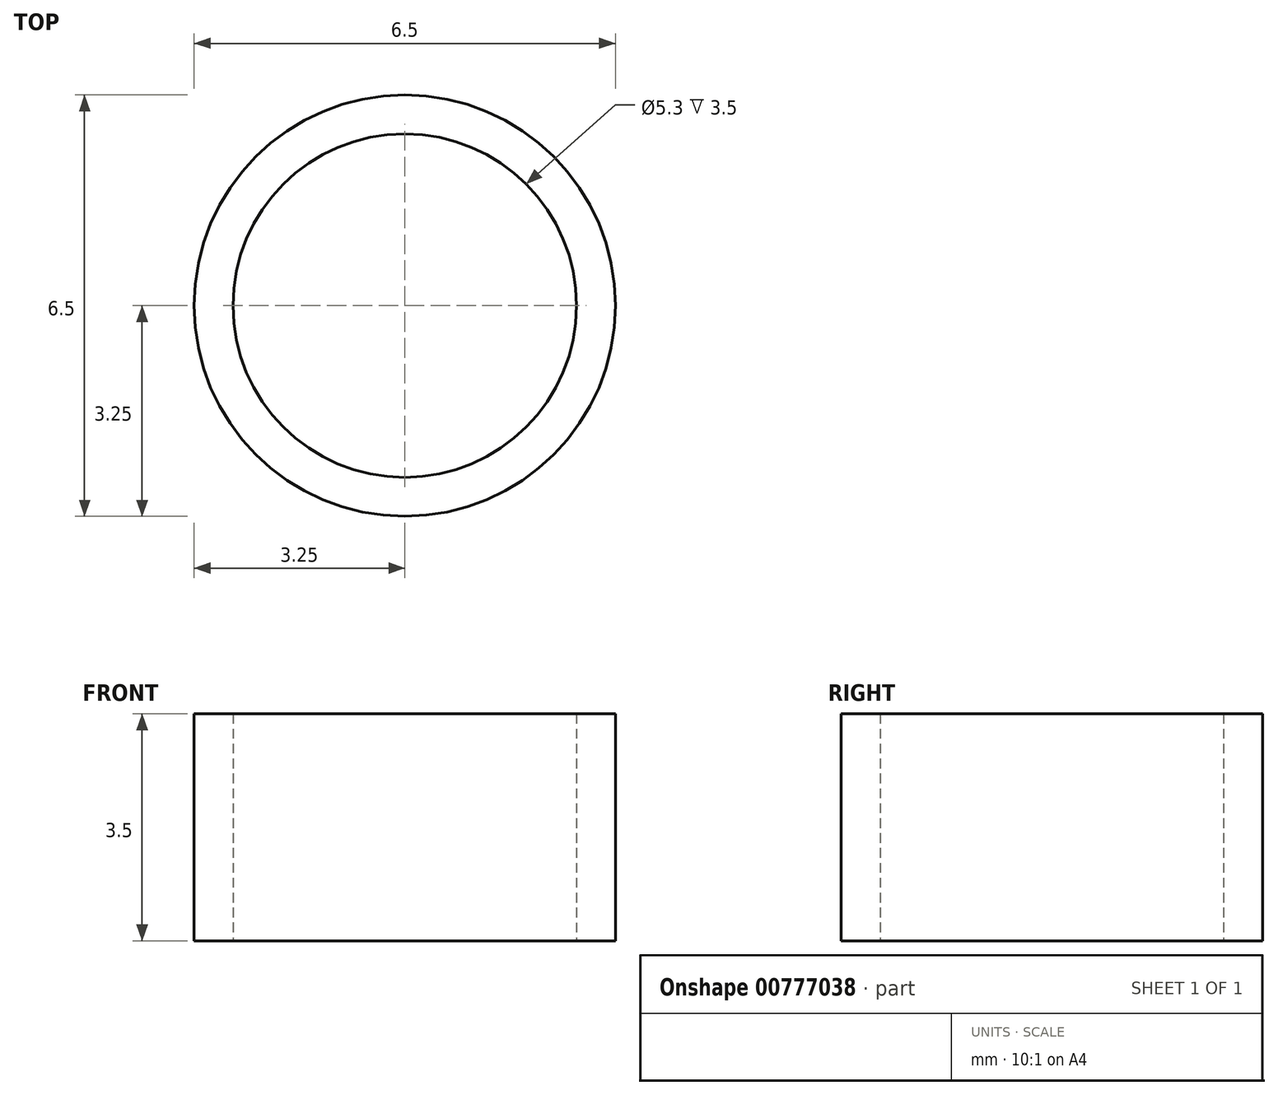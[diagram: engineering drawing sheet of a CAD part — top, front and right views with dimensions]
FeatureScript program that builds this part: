
annotation { "Feature Type Name" : "Feature", "Feature Type Description" : "" }
export const myFeature = defineFeature(function(context is Context, id is Id, definition is map)
    precondition{}
    {
        {
            var Q0;
            Q0=qCreatedBy(makeId("Top.planeOp"),FACE);
            var sketch = newSketch(context, id + "F0", { "sketchPlane" : qUnion([Q0])});
            skCircle(sketch, "E0", {"center": v(0, 0) * mm, "radius": 2.65 * mm});
            skCircle(sketch, "E1", {"center": v(0, 0) * mm, "radius": 3.25 * mm});
            skSolve(sketch);
        }
        {
            var Q0;
            Q0=qSketchRegion(id+"F0",true);
            extrude(context, id + "F1", {"entities" : qUnion([Q0]), "depth" : 3.5 * mm, "offsetDistance" : 25 * mm});
        }
    });
